# Revit family: Plum Fix_Basin_Argent_Evo_Asymmetric_900mm_LH
name_source: partatom
category: Plumbing Fixtures
revit_build: Autodesk Revit 2016 (Build: 20190508_0715(x64)
units: mm (PartAtom-declared; Revit-internal decimal feet)

## family parameters
Always vertical = Yes
Cut with Voids When Loaded = Yes
OmniClass Number = 23.45.05.14.14
OmniClass Title = Sinks/Lavatories
Part Type = Normal
Room Calculation Point = No
Round Connector Dimension = Use Diameter
Shared = No
Work Plane-Based = No

## types (1)
- 1 Tap Hole - LH
    Body Material = z_Argent_Ceramic White
    CW Connection = No
    CWFU = 0
    Cost = 0 $
    Description = Evo 900mm asymmetric basin
    HW Connection = No
    HWFU = 0
    IfcExportAs = IfcSanitaryTerminalType
    IfcExportType = SINK
    Manufacturer = Argent
    Manufacturer_Overall Depth = 460 mm  [stored 1.50919 ft]
    Manufacturer_Overall Height = 90 mm  [stored 0.295276 ft]
    Manufacturer_Overall Width = 905 mm  [stored 2.96916 ft]
    Manufacturer_Spec Code = EV36MUL01
    Manufacturer_URL__Product Specific = https://www.argentaust.com.au
    Model = EV36MUL01
    ModifiedIssue_ANZRS = 20191125 $
    Type Comments = 1 Tap Hole
    URL = https://www.argentaust.com.au
    Uniclass2015Code = Pr_40_20_96_81
    Uniclass2015Title = Sinks
    Uniclass2015Version = Products v1.13
    Vent Connection = No
    WFU = 0
    Waste Connection = Yes

note: [stored X ft] marks values corroborated as IEEE doubles in the binary element streams (Revit-internal decimal feet)

## geometry (parser evidence)
native form markers: Sweep x3
no freeform markers — native parametric forms only
